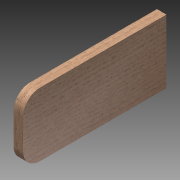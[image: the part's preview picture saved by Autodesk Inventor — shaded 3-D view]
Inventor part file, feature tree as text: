
AUTODESK INVENTOR PART (.ipt)
format: ipt  version: 2013 (Build 170138000, 138)  size: 98,816 bytes
history: native  units: in
note: dims shown in document units (in); Inventor stores cm internally (conversion verified against a paired STEP export)
features: extrude x1, fillet x1, sketch x1
ambient origin geometry x8: Origin, YZ Plane, XZ Plane, XY Plane, X Axis, Y Axis, Z Axis, Center Point
bodies: Solid1 (feature_tree)
feature tree (3):
  extrude  "Extrusion1"  Depth=0.75in
  fillet  "Fillet1"  Radius=11.25in
  sketch  "Sketch1"  dims[d0=5.0in d1=0.75in d2=11.25in d3=0.0in d4=1.3125in]
